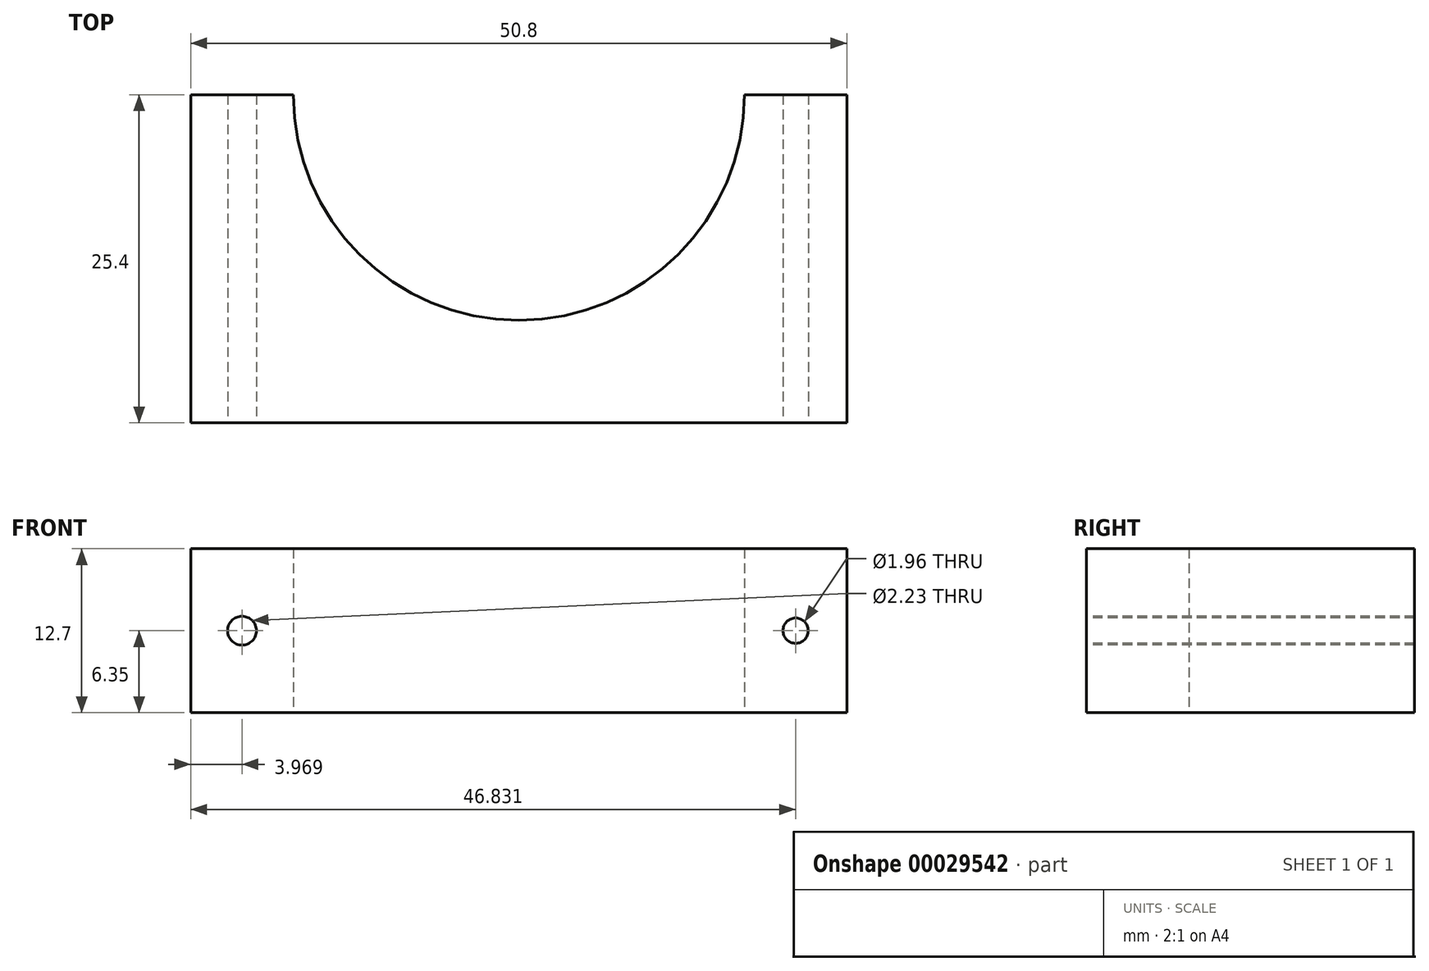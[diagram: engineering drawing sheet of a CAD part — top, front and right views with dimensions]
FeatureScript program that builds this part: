
annotation { "Feature Type Name" : "Feature", "Feature Type Description" : "" }
export const myFeature = defineFeature(function(context is Context, id is Id, definition is map)
    precondition{}
    {
        {
            var Q0;
            Q0=qCreatedBy(makeId("Top.planeOp"),FACE);
            var sketch = newSketch(context, id + "F0", { "sketchPlane" : qUnion([Q0])});
            skLineSegment(sketch, "E0.rect.top", {"start": v(25.4, -12.7) * mm, "end": v(-25.4, -12.7) * mm});
            skLineSegment(sketch, "E0.rect.left", {"start": v(25.4, 12.7) * mm, "end": v(25.4, -12.7) * mm});
            skLineSegment(sketch, "E0.rect.right", {"start": v(-25.4, 12.7) * mm, "end": v(-25.4, -12.7) * mm});
            skPoint(sketch, "E0.rect.middle", {"position": v(0, 0) * mm});
            skArc(sketch, "E1", {"start": v(-17.46, 12.7) * mm, "mid": v(0, -4.76) * mm, "end": v(17.46, 12.7) * mm});
            skLineSegment(sketch, "E2", {"start": v(-25.4, 12.7) * mm, "end": v(-17.46, 12.7) * mm});
            skLineSegment(sketch, "E3", {"start": v(17.46, 12.7) * mm, "end": v(25.4, 12.7) * mm});
            skSolve(sketch);
        }
        {
            var Q0;
            Q0 = qSketchRegion(id + "F0", true);
            extrude(context, id + "F1", {"entities" : qUnion([Q0]), "depth" : 12.7 * mm});
        }
        {
            var Q0;
            Q0=makeQuery(id+"F1.opExtrude","SWEPT_FACE",FACE,{"disambiguationData":[OSD([sQuery(id+"F0.wireOp",EDGE,"E0.rect.top")])]});
            var sketch = newSketch(context, id + "F2", { "sketchPlane" : qUnion([Q0])});
            skLineSegment(sketch, "E4", {"start": v(-25.4, 6.35) * mm, "end": v(25.4, 6.35) * mm, "construction": true});
            skLineSegment(sketch, "E5", {"start": v(0, 12.7) * mm, "end": v(0, 0) * mm, "construction": true});
            skCircle(sketch, "E6", {"center": v(-21.43, 6.35) * mm, "radius": 1.12 * mm});
            skCircle(sketch, "E7", {"center": v(21.43, 6.35) * mm, "radius": 0.98 * mm});
            skSolve(sketch);
        }
        {
            var Q0;
            Q0 = qSketchRegion(id + "F2", true);
            extrude(context, id + "F3", {"entities" : qUnion([Q0]), "operationType" : NewBodyOperationType.REMOVE, "oppositeDirection" : true, "depth" : 50.8 * mm});
        }
    });
